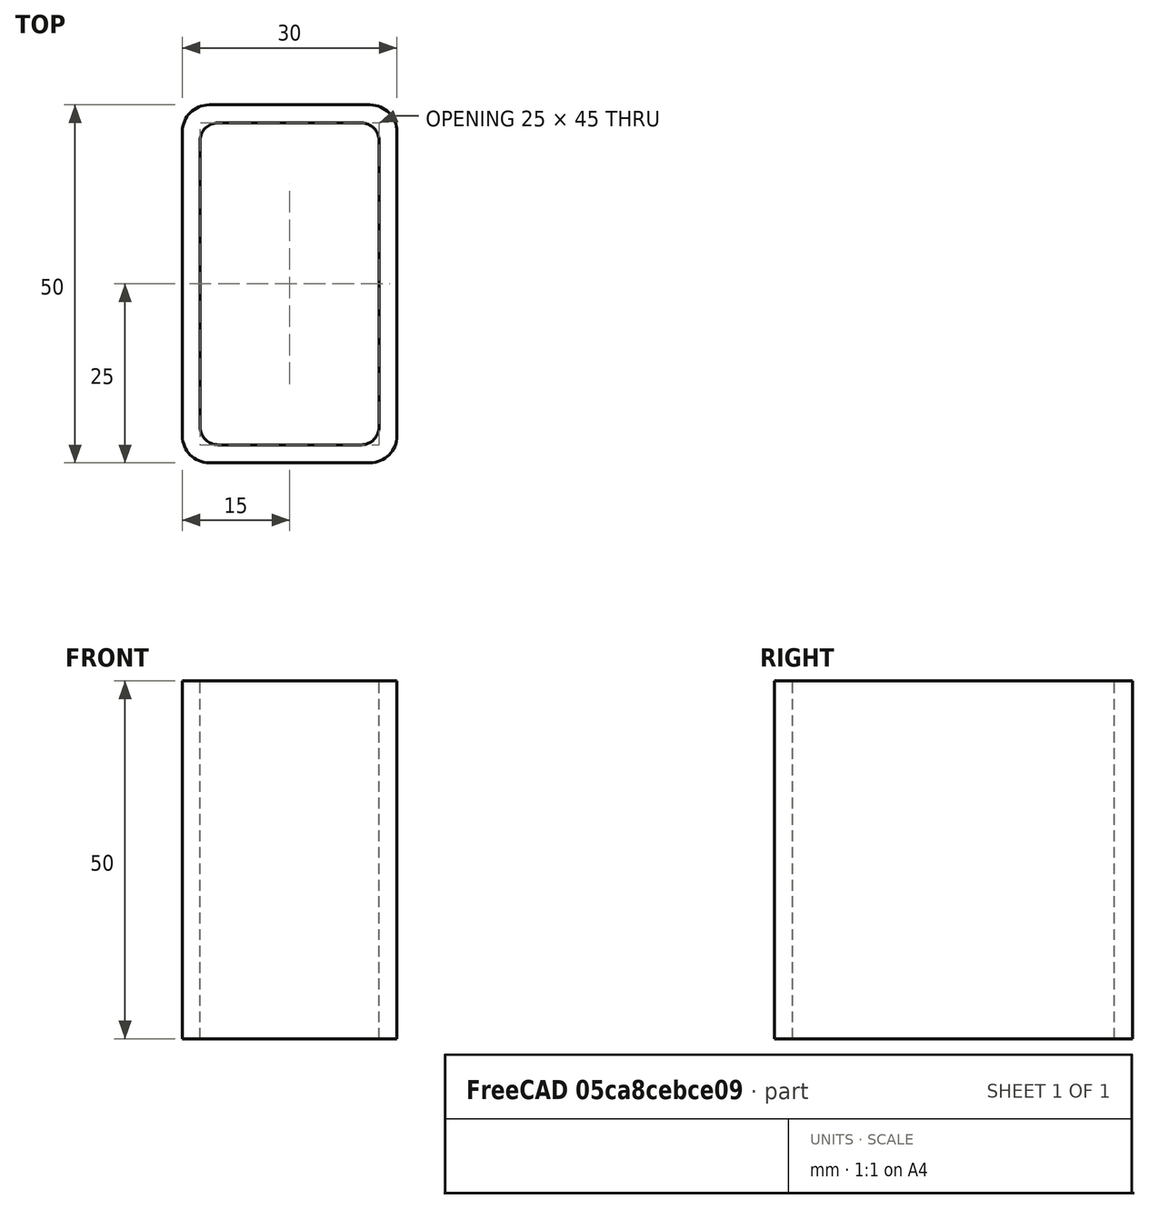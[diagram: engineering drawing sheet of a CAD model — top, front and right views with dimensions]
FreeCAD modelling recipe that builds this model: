
FCSTD DOCUMENT  (FreeCAD 0.15R4671 (Git))
Label: Rectangular hollow section 50x30x2.5 EN10219 S235JRH
License: All rights reserved
LicenseURL: http://en.wikipedia.org/wiki/All_rights_reserved
objects: Sketcher::SketchObject×1, Part::Extrusion×1
note: 2 computed .brp shape members not serialized (recipe doc carries the construction recipe); baked Part::Feature solids carry a one-line shape summary decoded from their .brp

FEATURE [Sketcher::SketchObject] Sketch
  sketch-geometry (16):
    g0: LineSegment StartX=-10 StartY=22.5 StartZ=0 EndX=10 EndY=22.5 EndZ=0
    g1: LineSegment StartX=12.5 StartY=20 StartZ=0 EndX=12.5 EndY=-20 EndZ=0
    g2: LineSegment StartX=10 StartY=-22.5 StartZ=0 EndX=-10 EndY=-22.5 EndZ=0
    g3: LineSegment StartX=-12.5 StartY=-20 StartZ=0 EndX=-12.5 EndY=20 EndZ=0
    g4: LineSegment StartX=-11.25 StartY=25 StartZ=0 EndX=11.25 EndY=25 EndZ=0
    g5: LineSegment StartX=15 StartY=21.25 StartZ=0 EndX=15 EndY=-21.25 EndZ=0
    g6: LineSegment StartX=11.25 StartY=-25 StartZ=0 EndX=-11.25 EndY=-25 EndZ=0
    g7: LineSegment StartX=-15 StartY=-21.25 StartZ=0 EndX=-15 EndY=21.25 EndZ=0
    g8: ArcOfCircle CenterX=-10 CenterY=20 CenterZ=0 NormalX=0 NormalY=0 NormalZ=1 Radius=2.5 StartAngle=1.5708 EndAngle=3.14159
    g9: ArcOfCircle CenterX=10 CenterY=20 CenterZ=0 NormalX=0 NormalY=0 NormalZ=1 Radius=2.5 StartAngle=0 EndAngle=1.5708
    g10: ArcOfCircle CenterX=10 CenterY=-20 CenterZ=0 NormalX=0 NormalY=0 NormalZ=1 Radius=2.5 StartAngle=4.71239 EndAngle=6.28319
    g11: ArcOfCircle CenterX=-10 CenterY=-20 CenterZ=0 NormalX=0 NormalY=0 NormalZ=1 Radius=2.5 StartAngle=3.14159 EndAngle=4.71239
    g12: ArcOfCircle CenterX=11.25 CenterY=21.25 CenterZ=0 NormalX=0 NormalY=0 NormalZ=1 Radius=3.75 StartAngle=0 EndAngle=1.5708
    g13: ArcOfCircle CenterX=11.25 CenterY=-21.25 CenterZ=0 NormalX=0 NormalY=0 NormalZ=1 Radius=3.75 StartAngle=4.71239 EndAngle=6.28319
    g14: ArcOfCircle CenterX=-11.25 CenterY=-21.25 CenterZ=0 NormalX=0 NormalY=0 NormalZ=1 Radius=3.75 StartAngle=3.14159 EndAngle=4.71239
    g15: ArcOfCircle CenterX=-11.25 CenterY=21.25 CenterZ=0 NormalX=0 NormalY=0 NormalZ=1 Radius=3.75 StartAngle=1.5708 EndAngle=3.14159
  constraints (36):
    c: Horizontal(g2)
    c: Vertical(g3)
    c: Horizontal(g6)
    c: Vertical(g7)
    c: Tangent(g3,g8) = 1.5708
    c: Tangent(g0,g8) = 1.5708
    c: Tangent(g0,g9) = 1.5708
    c: Tangent(g1,g9) = 1.5708
    c: Tangent(g1,g10) = 1.5708
    c: Tangent(g2,g10) = 1.5708
    c: Tangent(g2,g11) = 1.5708
    c: Tangent(g3,g11) = 1.5708
    c: Tangent(g4,g12) = 1.5708
    c: Tangent(g5,g12) = 1.5708
    c: Tangent(g5,g13) = 1.5708
    c: Tangent(g6,g13) = 1.5708
    c: Tangent(g6,g14) = 1.5708
    c: Tangent(g7,g14) = 1.5708
    c: Tangent(g7,g15) = 1.5708
    c: Tangent(g4,g15) = 1.5708
    c: Equal(g9,g8)
    c: Equal(g9,g11)
    c: Equal(g9,g10)
    c: Equal(g12,g15)
    c: Equal(g12,g14)
    c: Equal(g12,g13)
    c: Symmetric(g4,g6,g-1)
    c: Symmetric(g7,g5,g-2)
    c: DistanceY(g4,g6) = -50
    c: DistanceX(g7,g5) = 30
    c: Symmetric(g3,g1,g-2)
    c: Symmetric(g0,g2,g-1)
    c: DistanceY(g0,g4) = 2.5
    c: DistanceX(g5,g1) = -2.5
    c: Radius(g9) = 2.5
    c: Radius(g12) = 3.75
FEATURE [Part::Extrusion] Extrude  label="Rectangular hollow section 50x30x2.5 EN10219 S235JRH"
  Base = -> Sketch
  Dir = (0,0,50)
  Solid = true
